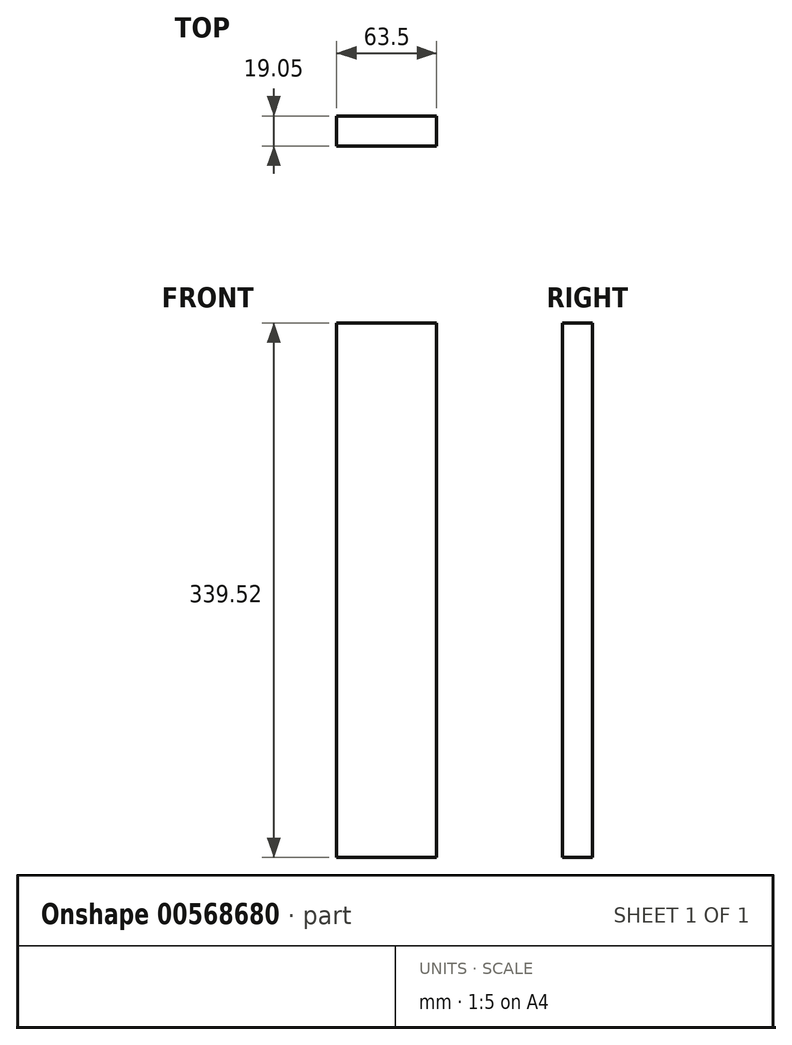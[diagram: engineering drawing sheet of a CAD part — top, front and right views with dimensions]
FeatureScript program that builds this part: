
annotation { "Feature Type Name" : "Feature", "Feature Type Description" : "" }
export const myFeature = defineFeature(function(context is Context, id is Id, definition is map)
    precondition{}
    {
        {
            var Q0;
            Q0=qCreatedBy(makeId("Front.planeOp"),FACE);
            var sketch = newSketch(context, id + "F0", { "sketchPlane" : qUnion([Q0])});
            skLineSegment(sketch, "E0.bottom", {"start": v(-31.75, 169.76) * mm, "end": v(31.75, 169.76) * mm});
            skLineSegment(sketch, "E0.top", {"start": v(-31.75, -169.76) * mm, "end": v(31.75, -169.76) * mm});
            skLineSegment(sketch, "E0.left", {"start": v(-31.75, 169.76) * mm, "end": v(-31.75, -169.76) * mm});
            skLineSegment(sketch, "E0.right", {"start": v(31.75, 169.76) * mm, "end": v(31.75, -169.76) * mm});
            skPoint(sketch, "E0.middle", {"position": v(0, 0) * mm});
            skSolve(sketch);
        }
        {
            var Q0;
            Q0=makeQuery(id+"F0.imprint","IMPRINT",FACE,{"disambiguationData":[TD([[makeQuery(id+"F0.imprint","IMPRINT",EDGE,{"derivedFrom":sQuery(id+"F0.wireOp",EDGE,"E0.bottom")}),-1.0]])]});
            extrude(context, id + "F1", {"entities" : qUnion([Q0]), "depth" : 19.05 * mm, "offsetDistance" : 25.4 * mm});
        }
    });
